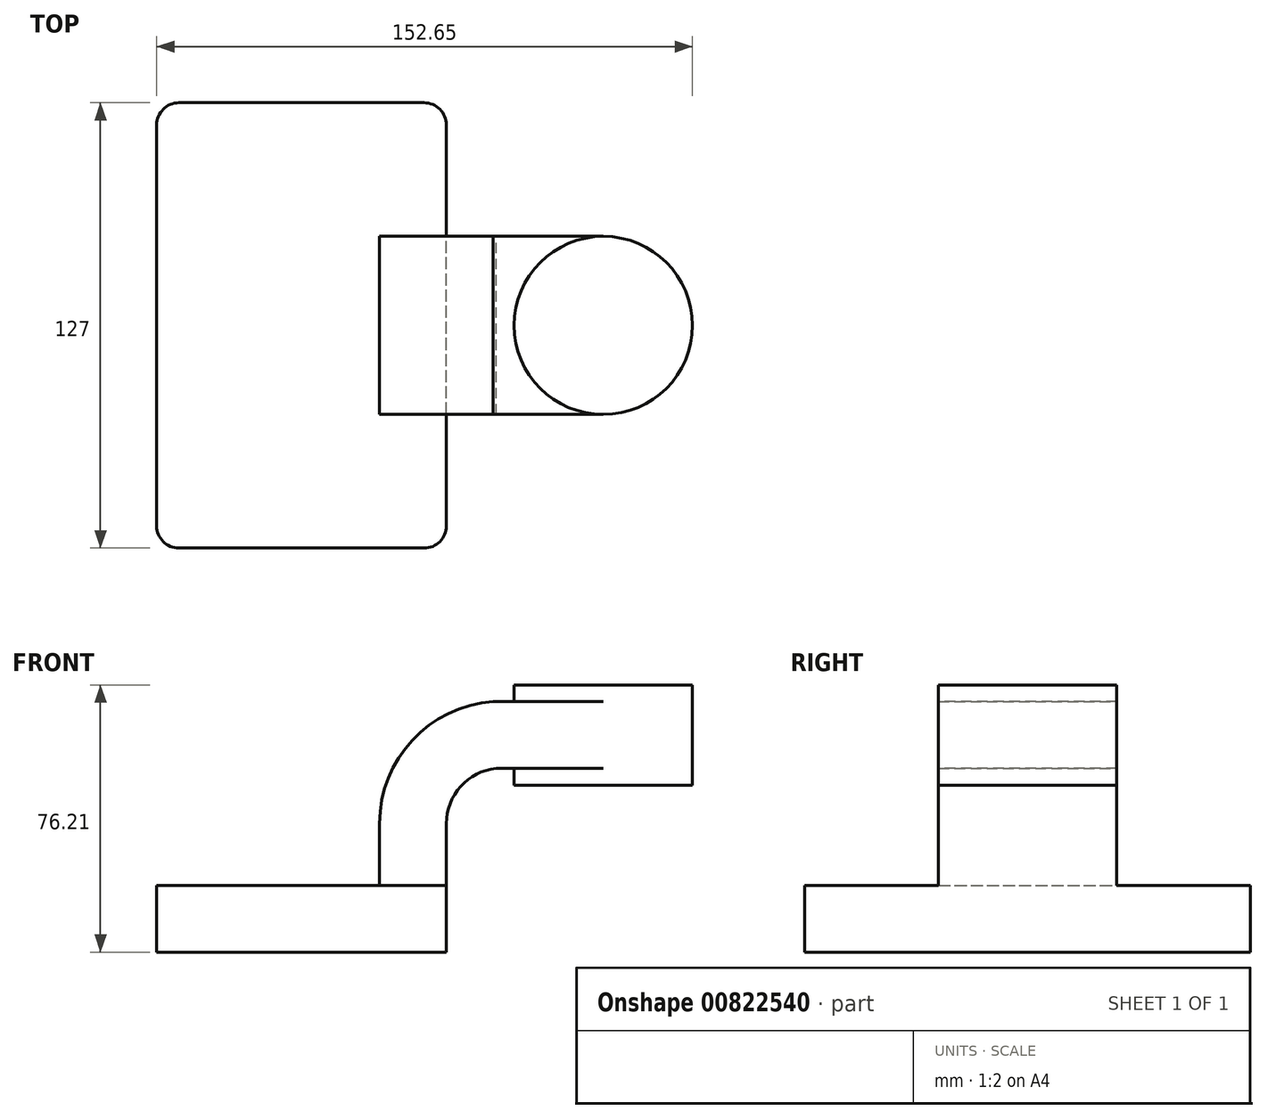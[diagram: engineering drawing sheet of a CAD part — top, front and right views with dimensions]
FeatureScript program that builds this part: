
annotation { "Feature Type Name" : "Feature", "Feature Type Description" : "" }
export const myFeature = defineFeature(function(context is Context, id is Id, definition is map)
    precondition{}
    {
        {
            var Q0;
            Q0=qCreatedBy(makeId("Front.planeOp"),FACE);
            var sketch = newSketch(context, id + "F0", { "sketchPlane" : qUnion([Q0])});
            skLineSegment(sketch, "E0.bottom", {"start": v(-41.27, -9.53) * mm, "end": v(41.27, -9.53) * mm});
            skLineSegment(sketch, "E0.top", {"start": v(-41.28, 9.53) * mm, "end": v(41.28, 9.53) * mm});
            skLineSegment(sketch, "E0.left", {"start": v(-41.27, -9.53) * mm, "end": v(-41.27, 9.52) * mm});
            skLineSegment(sketch, "E0.right", {"start": v(41.28, -9.53) * mm, "end": v(41.28, 9.52) * mm});
            skPoint(sketch, "E0.middle", {"position": v(0, 0) * mm});
            skLineSegment(sketch, "E1", {"start": v(41.28, 9.52) * mm, "end": v(41.28, 27.1) * mm});
            skArc(sketch, "E2", {"start": v(41.28, 27.1) * mm, "mid": v(45.34, 37.7) * mm, "end": v(55.45, 42.88) * mm});
            skPoint(sketch, "E2.endSnap0", {"position": v(58.8, 42.88) * mm});
            skLineSegment(sketch, "E3", {"start": v(55.45, 42.88) * mm, "end": v(85.98, 42.88) * mm});
            skLineSegment(sketch, "E4.bottom", {"start": v(60.58, 38.1) * mm, "end": v(111.38, 38.1) * mm});
            skLineSegment(sketch, "E4.top", {"start": v(60.58, 66.67) * mm, "end": v(111.38, 66.67) * mm});
            skLineSegment(sketch, "E4.left", {"start": v(60.58, 38.1) * mm, "end": v(60.58, 66.67) * mm});
            skLineSegment(sketch, "E4.right", {"start": v(111.38, 38.1) * mm, "end": v(111.38, 66.67) * mm});
            skPoint(sketch, "E4.middle", {"position": v(85.98, 52.39) * mm});
            skLineSegment(sketch, "E5.0", {"start": v(54.62, 61.93) * mm, "end": v(85.98, 61.93) * mm});
            skArc(sketch, "E5.1", {"start": v(22.23, 27.1) * mm, "mid": v(31.58, 50.88) * mm, "end": v(54.62, 61.93) * mm});
            skLineSegment(sketch, "E5.2", {"start": v(22.23, 9.52) * mm, "end": v(22.23, 27.1) * mm});
            skFitSpline(sketch, "E6", {"points": [v(-41.27, 9.52) * mm, v(54.62, 61.93) * mm], "startDerivative": vector(0.4, 109.15) * mm, "endDerivative": vector(147.94, -1.92) * mm});
            skLineSegment(sketch, "E7", {"start": v(85.98, 66.67) * mm, "end": v(85.98, 38.1) * mm});
            skSolve(sketch);
        }
        {
            var Q0;
            Q0=makeQuery(id+"F0.imprint","IMPRINT",FACE,{"disambiguationData":[TD([[makeQuery(id+"F0.imprint","IMPRINT",EDGE,{"derivedFrom":sQuery(id+"F0.wireOp",EDGE,"E0.bottom")}),1.0]])]});
            extrude(context, id + "F1", {"entities" : qUnion([Q0]), "endBound" : BoundingType.SYMMETRIC, "depth" : 127 * mm, "offsetDistance" : 25.4 * mm});
        }
        {
            var Q0;
            {var subQ1=sQuery(id+"F0.wireOp",EDGE,"E1");Q0=makeQuery(id+"F0.imprint","IMPRINT",FACE,{"disambiguationData":[TD([[makeQuery(id+"F0.imprint","IMPRINT",EDGE,{"derivedFrom":subQ1}),1.0]])]});}
            extrude(context, id + "F2", {"entities" : qUnion([Q0]), "operationType" : NewBodyOperationType.ADD, "endBound" : BoundingType.SYMMETRIC, "depth" : 50.8 * mm, "offsetDistance" : 25.4 * mm});
        }
        {
            var Q0;
            Q0=makeQuery(id+"F0.imprint","IMPRINT",FACE,{"disambiguationData":[TD([[makeQuery(id+"F0.imprint","IMPRINT",EDGE,{"derivedFrom":sQuery(id+"F0.wireOp",EDGE,"E5.1")}),1.0]])]});
            extrude(context, id + "F3", {"entities" : qUnion([Q0]), "operationType" : NewBodyOperationType.ADD, "endBound" : BoundingType.SYMMETRIC, "depth" : 15.88 * mm, "offsetDistance" : 25.4 * mm});
        }
        {
            var Q0;
            {var subQ0=sQuery(id+"F0.wireOp",EDGE,"E7");var subQ1=sQuery(id+"F0.wireOp",EDGE,"E3");var subQ2=makeQuery(id+"F0.imprint","INTERSECT",VERTEX,{"derivedFrom":[subQ1,subQ0]});Q0=makeQuery(id+"F0.imprint","IMPRINT",FACE,{"disambiguationData":[TD([[makeQuery(id+"F0.imprint","IMPRINT",EDGE,{"disambiguationData":[TD([[subQ2,1.0]])],"derivedFrom":subQ1}),1.0]])]});}
            extrude(context, id + "F4", {"entities" : qUnion([Q0]), "operationType" : NewBodyOperationType.ADD, "endBound" : BoundingType.SYMMETRIC, "depth" : 50.8 * mm, "offsetDistance" : 25.4 * mm});
        }
        {
            var Q0;
            {var subQ0=sQuery(id+"F0.wireOp",EDGE,"E4.right");Q0=makeQuery(id+"F0.imprint","IMPRINT",FACE,{"disambiguationData":[TD([[makeQuery(id+"F0.imprint","IMPRINT",EDGE,{"derivedFrom":subQ0}),1.0]])]});}
            var Q1;
            Q1=sQuery(id+"F0.wireOp",EDGE,"E7");
            revolve(context, id + "F5", {"operationType" : NewBodyOperationType.ADD, "surfaceOperationType" : NewSurfaceOperationType.NEW, "entities" : qUnion([Q0]), "axis" : qUnion([Q1]), "revolveType" : RevolveType.FULL});
        }
        {
            var Q0;
            Q0=makeQuery(id+"F1.opExtrude","CAP_EDGE",EDGE,{"disambiguationData":[OSD([sQuery(id+"F0.wireOp",EDGE,"E0.right")])],"isStart":false});
            var Q1;
            Q1=makeQuery(id+"F1.opExtrude","CAP_EDGE",EDGE,{"disambiguationData":[OSD([sQuery(id+"F0.wireOp",EDGE,"E0.left")])],"isStart":false});
            var Q2;
            Q2=makeQuery(id+"F1.opExtrude","CAP_EDGE",EDGE,{"disambiguationData":[OSD([sQuery(id+"F0.wireOp",EDGE,"E0.right")])],"isStart":true});
            var Q3;
            Q3=makeQuery(id+"F1.opExtrude","CAP_EDGE",EDGE,{"disambiguationData":[OSD([sQuery(id+"F0.wireOp",EDGE,"E0.left")])],"isStart":true});
            fillet(context, id + "F6", {"entities" : qUnion([Q0, Q1, Q2, Q3]), "radius" : 6.35 * mm, "tangentPropagation" : true, "allowEdgeOverflow" : false});
        }
    });
